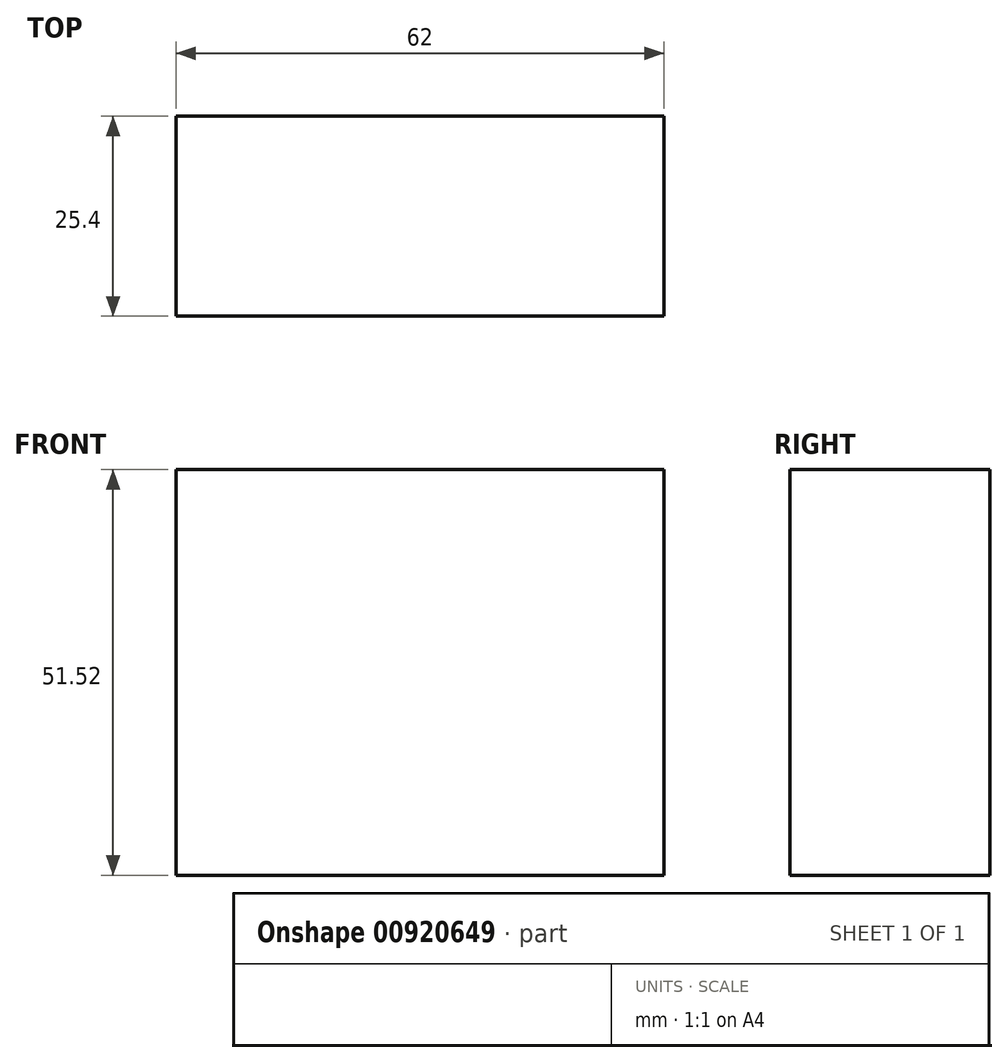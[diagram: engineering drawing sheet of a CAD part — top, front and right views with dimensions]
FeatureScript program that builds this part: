
annotation { "Feature Type Name" : "Feature", "Feature Type Description" : "" }
export const myFeature = defineFeature(function(context is Context, id is Id, definition is map)
    precondition{}
    {
        {
            var Q0;
            Q0=qCreatedBy(makeId("Front.planeOp"),FACE);
            var sketch = newSketch(context, id + "F0", { "sketchPlane" : qUnion([Q0])});
            skLineSegment(sketch, "E0.bottom", {"start": v(0, 13) * mm, "end": v(0, 13) * mm});
            skLineSegment(sketch, "E0.top", {"start": v(0, 0) * mm, "end": v(0, 0) * mm});
            skLineSegment(sketch, "E1.bottom", {"start": v(-29.47, 28.49) * mm, "end": v(32.53, 28.49) * mm});
            skLineSegment(sketch, "E1.top", {"start": v(-29.47, -23.03) * mm, "end": v(32.53, -23.03) * mm});
            skLineSegment(sketch, "E1.left", {"start": v(-29.47, 28.49) * mm, "end": v(-29.47, -23.03) * mm});
            skLineSegment(sketch, "E1.right", {"start": v(32.53, 28.49) * mm, "end": v(32.53, -23.03) * mm});
            skSolve(sketch);
        }
        {
            var Q0;
            Q0 = qSketchRegion(id + "F0", true);
            extrude(context, id + "F1", {"entities" : qUnion([Q0]), "depth" : 25.4 * mm, "offsetDistance" : 25.4 * mm});
        }
    });
